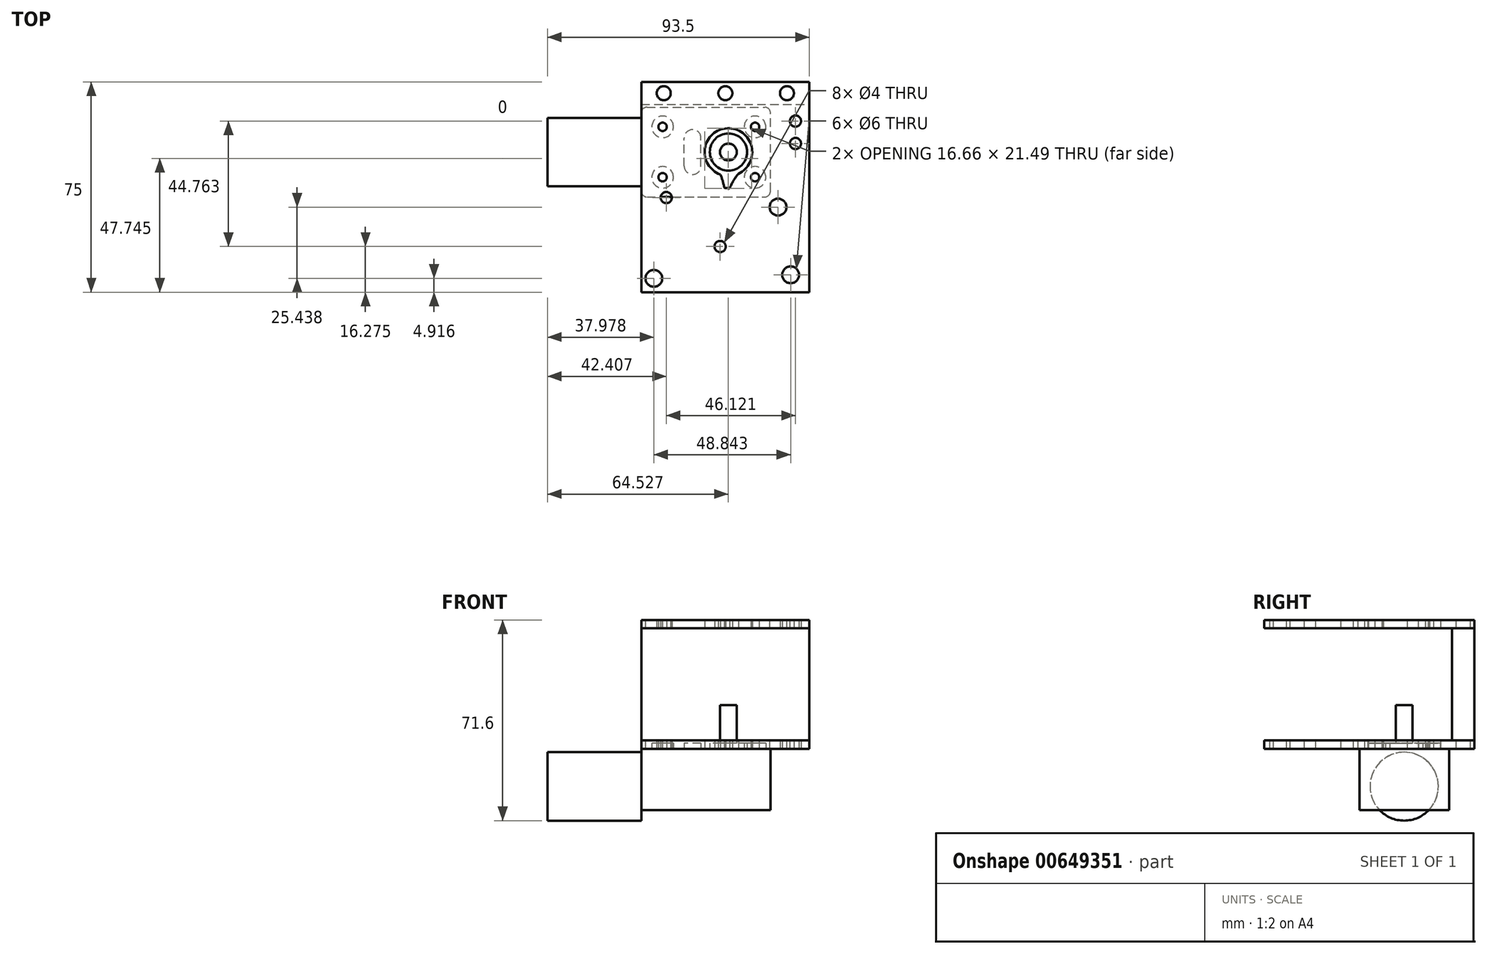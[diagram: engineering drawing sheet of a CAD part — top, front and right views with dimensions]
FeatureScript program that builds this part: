
annotation { "Feature Type Name" : "Feature", "Feature Type Description" : "" }
export const myFeature = defineFeature(function(context is Context, id is Id, definition is map)
    precondition{}
    {
        {
            var Q0;
            Q0=qCreatedBy(makeId("Top.planeOp"),FACE);
            var sketch = newSketch(context, id + "F0", { "sketchPlane" : qUnion([Q0])});
            skCircle(sketch, "E0", {"center": v(0, 0) * mm, "radius": 3 * mm});
            skCircle(sketch, "E1", {"center": v(0, 0) * mm, "radius": 6.65 * mm});
            skLineSegment(sketch, "E2.bottom", {"start": v(-29.1, -16) * mm, "end": v(13, -16) * mm});
            skLineSegment(sketch, "E2.top", {"start": v(-29.1, 16) * mm, "end": v(13, 16) * mm});
            skLineSegment(sketch, "E2.left", {"start": v(-31.1, -14) * mm, "end": v(-31.1, 14) * mm});
            skLineSegment(sketch, "E2.right", {"start": v(15, -14) * mm, "end": v(15, 14) * mm});
            skLineSegment(sketch, "E3", {"start": v(-31.1, 0) * mm, "end": v(15, 0) * mm, "construction": true});
            skLineSegment(sketch, "E4.bottom", {"start": v(-23.5, -9) * mm, "end": v(9.5, -9) * mm, "construction": true});
            skLineSegment(sketch, "E4.top", {"start": v(-23.5, 9) * mm, "end": v(9.5, 9) * mm, "construction": true});
            skLineSegment(sketch, "E4.left", {"start": v(-23.5, -9) * mm, "end": v(-23.5, 9) * mm, "construction": true});
            skLineSegment(sketch, "E4.right", {"start": v(9.5, -9) * mm, "end": v(9.5, 9) * mm, "construction": true});
            skCircle(sketch, "E5", {"center": v(-23.5, 9) * mm, "radius": 1.5 * mm});
            skCircle(sketch, "E6", {"center": v(-23.5, -9) * mm, "radius": 1.5 * mm});
            skCircle(sketch, "E7", {"center": v(9.5, 9) * mm, "radius": 1.5 * mm});
            skCircle(sketch, "E8", {"center": v(9.5, -9) * mm, "radius": 1.5 * mm});
            skCircle(sketch, "E9", {"center": v(-23.5, 9) * mm, "radius": 3.85 * mm});
            skCircle(sketch, "E10", {"center": v(9.5, 9) * mm, "radius": 3.85 * mm});
            skCircle(sketch, "E11", {"center": v(9.5, -9) * mm, "radius": 3.85 * mm});
            skCircle(sketch, "E12", {"center": v(-23.5, -9) * mm, "radius": 3.85 * mm});
            skPoint(sketch, "E13", {"position": v(9.5, 0) * mm});
            skLineSegment(sketch, "E14.left", {"start": v(-15.8, -5) * mm, "end": v(-15.8, 5) * mm});
            skLineSegment(sketch, "E14.right", {"start": v(-9.8, -5) * mm, "end": v(-9.8, 5) * mm});
            skArc(sketch, "E15", {"start": v(-9.8, 5) * mm, "mid": v(-12.8, 8) * mm, "end": v(-15.8, 5) * mm});
            skArc(sketch, "E16", {"start": v(-15.8, -5) * mm, "mid": v(-12.8, -8) * mm, "end": v(-9.8, -5) * mm});
            skPoint(sketch, "E17", {"position": v(-15.8, 0) * mm});
            skPoint(sketch, "E18.visualSharp", {"position": v(15, 16) * mm});
            skArc(sketch, "E18.filletArc", {"start": v(15, 14) * mm, "mid": v(14.41, 15.41) * mm, "end": v(13, 16) * mm});
            skPoint(sketch, "E19.visualSharp", {"position": v(15, -16) * mm});
            skArc(sketch, "E19.filletArc", {"start": v(13, -16) * mm, "mid": v(14.41, -15.41) * mm, "end": v(15, -14) * mm});
            skPoint(sketch, "E20.visualSharp", {"position": v(-31.1, 16) * mm});
            skArc(sketch, "E20.filletArc", {"start": v(-29.1, 16) * mm, "mid": v(-30.51, 15.41) * mm, "end": v(-31.1, 14) * mm});
            skPoint(sketch, "E21.visualSharp", {"position": v(-31.1, -16) * mm});
            skArc(sketch, "E21.filletArc", {"start": v(-31.1, -14) * mm, "mid": v(-30.51, -15.41) * mm, "end": v(-29.1, -16) * mm});
            skSolve(sketch);
        }
        {
            var Q0;
            Q0 = qSketchRegion(id + "F0", true);
            var Q1;
            Q1=makeQuery(id+"F0.imprint","IMPRINT",FACE,{"disambiguationData":[TD([[makeQuery(id+"F0.imprint","IMPRINT",EDGE,{"derivedFrom":sQuery(id+"F0.wireOp",EDGE,"E6")}),-1.0]])]});
            var Q2;
            Q2=makeQuery(id+"F0.imprint","IMPRINT",FACE,{"disambiguationData":[TD([[makeQuery(id+"F0.imprint","IMPRINT",EDGE,{"derivedFrom":sQuery(id+"F0.wireOp",EDGE,"E14.left")}),-1.0]])]});
            var Q3;
            Q3=makeQuery(id+"F0.imprint","IMPRINT",FACE,{"disambiguationData":[TD([[makeQuery(id+"F0.imprint","IMPRINT",EDGE,{"derivedFrom":sQuery(id+"F0.wireOp",EDGE,"E0")}),-1.0]])]});
            var Q4;
            Q4=makeQuery(id+"F0.imprint","IMPRINT",FACE,{"disambiguationData":[TD([[makeQuery(id+"F0.imprint","IMPRINT",EDGE,{"derivedFrom":sQuery(id+"F0.wireOp",EDGE,"E0")}),1.0]])]});
            var Q5;
            Q5=makeQuery(id+"F0.imprint","IMPRINT",FACE,{"disambiguationData":[TD([[makeQuery(id+"F0.imprint","IMPRINT",EDGE,{"derivedFrom":sQuery(id+"F0.wireOp",EDGE,"E7")}),1.0]])]});
            var Q6;
            Q6=makeQuery(id+"F0.imprint","IMPRINT",FACE,{"disambiguationData":[TD([[makeQuery(id+"F0.imprint","IMPRINT",EDGE,{"derivedFrom":sQuery(id+"F0.wireOp",EDGE,"E8")}),-1.0]])]});
            var Q7;
            Q7=makeQuery(id+"F0.imprint","IMPRINT",FACE,{"disambiguationData":[TD([[makeQuery(id+"F0.imprint","IMPRINT",EDGE,{"derivedFrom":sQuery(id+"F0.wireOp",EDGE,"E8")}),1.0]])]});
            var Q8;
            Q8=makeQuery(id+"F0.imprint","IMPRINT",FACE,{"disambiguationData":[TD([[makeQuery(id+"F0.imprint","IMPRINT",EDGE,{"derivedFrom":sQuery(id+"F0.wireOp",EDGE,"E7")}),-1.0]])]});
            var Q9;
            Q9=makeQuery(id+"F0.imprint","IMPRINT",FACE,{"disambiguationData":[TD([[makeQuery(id+"F0.imprint","IMPRINT",EDGE,{"derivedFrom":sQuery(id+"F0.wireOp",EDGE,"E5")}),-1.0]])]});
            var Q10;
            Q10=makeQuery(id+"F0.imprint","IMPRINT",FACE,{"disambiguationData":[TD([[makeQuery(id+"F0.imprint","IMPRINT",EDGE,{"derivedFrom":sQuery(id+"F0.wireOp",EDGE,"E6")}),1.0]])]});
            var Q11;
            Q11=makeQuery(id+"F0.imprint","IMPRINT",FACE,{"disambiguationData":[TD([[makeQuery(id+"F0.imprint","IMPRINT",EDGE,{"derivedFrom":sQuery(id+"F0.wireOp",EDGE,"E5")}),1.0]])]});
            extrude(context, id + "F1", {"entities" : qUnion([Q0, Q1, Q2, Q3, Q4, Q5, Q6, Q7, Q8, Q9, Q10, Q11]), "oppositeDirection" : true, "depth" : 21.8 * mm, "offsetDistance" : 25 * mm});
        }
        {
            var Q0;
            Q0=makeQuery(id+"F0.imprint","IMPRINT",FACE,{"disambiguationData":[TD([[makeQuery(id+"F0.imprint","IMPRINT",EDGE,{"derivedFrom":sQuery(id+"F0.wireOp",EDGE,"E6")}),-1.0]])]});
            var Q1;
            Q1=makeQuery(id+"F0.imprint","IMPRINT",FACE,{"disambiguationData":[TD([[makeQuery(id+"F0.imprint","IMPRINT",EDGE,{"derivedFrom":sQuery(id+"F0.wireOp",EDGE,"E5")}),-1.0]])]});
            var Q2;
            Q2=makeQuery(id+"F0.imprint","IMPRINT",FACE,{"disambiguationData":[TD([[makeQuery(id+"F0.imprint","IMPRINT",EDGE,{"derivedFrom":sQuery(id+"F0.wireOp",EDGE,"E14.left")}),-1.0]])]});
            var Q3;
            Q3=makeQuery(id+"F0.imprint","IMPRINT",FACE,{"disambiguationData":[TD([[makeQuery(id+"F0.imprint","IMPRINT",EDGE,{"derivedFrom":sQuery(id+"F0.wireOp",EDGE,"E0")}),-1.0]])]});
            var Q4;
            Q4=makeQuery(id+"F0.imprint","IMPRINT",FACE,{"disambiguationData":[TD([[makeQuery(id+"F0.imprint","IMPRINT",EDGE,{"derivedFrom":sQuery(id+"F0.wireOp",EDGE,"E7")}),-1.0]])]});
            var Q5;
            Q5=makeQuery(id+"F0.imprint","IMPRINT",FACE,{"disambiguationData":[TD([[makeQuery(id+"F0.imprint","IMPRINT",EDGE,{"derivedFrom":sQuery(id+"F0.wireOp",EDGE,"E8")}),-1.0]])]});
            extrude(context, id + "F2", {"entities" : qUnion([Q0, Q1, Q2, Q3, Q4, Q5]), "operationType" : NewBodyOperationType.ADD, "depth" : 2 * mm, "offsetDistance" : 25 * mm});
        }
        {
            var Q0;
            Q0=makeQuery(id+"F0.imprint","IMPRINT",FACE,{"disambiguationData":[TD([[makeQuery(id+"F0.imprint","IMPRINT",EDGE,{"derivedFrom":sQuery(id+"F0.wireOp",EDGE,"E0")}),1.0]])]});
            extrude(context, id + "F3", {"entities" : qUnion([Q0]), "operationType" : NewBodyOperationType.ADD, "depth" : 15.6 * mm, "offsetDistance" : 25 * mm});
        }
        {
            var Q0;
            Q0=makeQuery(id+"F1.opExtrude","SWEPT_FACE",FACE,{"disambiguationData":[OSD([sQuery(id+"F0.wireOp",EDGE,"E2.left")])]});
            var sketch = newSketch(context, id + "F4", { "sketchPlane" : qUnion([Q0])});
            skLineSegment(sketch, "E22", {"start": v(0, 0) * mm, "end": v(0, -21.8) * mm, "construction": true});
            skCircle(sketch, "E23", {"center": v(0, -13.4) * mm, "radius": 12.2 * mm});
            skSolve(sketch);
        }
        {
            var Q0;
            Q0 = qSketchRegion(id + "F4", true);
            extrude(context, id + "F5", {"entities" : qUnion([Q0]), "operationType" : NewBodyOperationType.ADD, "depth" : 33.5 * mm, "offsetDistance" : 25 * mm});
        }
        {
            var Q0;
            Q0=qCreatedBy(makeId("Top.planeOp"),FACE);
            var sketch = newSketch(context, id + "F6", { "sketchPlane" : qUnion([Q0])});
            skCircle(sketch, "E24", {"center": v(0, 0) * mm, "radius": 8.5 * mm});
            skCircle(sketch, "E25.0", {"center": v(9.5, 9) * mm, "radius": 1.5 * mm});
            skCircle(sketch, "E25.1", {"center": v(9.5, -9) * mm, "radius": 1.5 * mm});
            skCircle(sketch, "E25.2", {"center": v(-23.5, -9) * mm, "radius": 1.5 * mm});
            skCircle(sketch, "E25.3", {"center": v(-23.5, 9) * mm, "radius": 1.5 * mm});
            skLineSegment(sketch, "E26.bottom", {"start": v(-31.1, 25) * mm, "end": v(28.9, 25) * mm});
            skLineSegment(sketch, "E26.top", {"start": v(-31.1, -50) * mm, "end": v(28.9, -50) * mm});
            skLineSegment(sketch, "E26.left", {"start": v(-31.1, 25) * mm, "end": v(-31.1, -50) * mm});
            skLineSegment(sketch, "E26.right", {"start": v(28.9, 25) * mm, "end": v(28.9, -50) * mm});
            skLineSegment(sketch, "E27.top", {"start": v(-31.1, 17) * mm, "end": v(28.9, 17) * mm});
            skLineSegment(sketch, "E27.left", {"start": v(-31.1, 25) * mm, "end": v(-31.1, 17) * mm});
            skLineSegment(sketch, "E27.right", {"start": v(28.9, 25) * mm, "end": v(28.9, 17) * mm});
            skCircle(sketch, "E28", {"center": v(9.5, 9) * mm, "radius": 2 * mm, "construction": true});
            skCircle(sketch, "E29", {"center": v(9.5, -9) * mm, "radius": 2 * mm, "construction": true});
            skCircle(sketch, "E30", {"center": v(-23.5, 9) * mm, "radius": 2 * mm, "construction": true});
            skCircle(sketch, "E31", {"center": v(-23.5, -9) * mm, "radius": 2 * mm, "construction": true});
            skLineSegment(sketch, "E32.0", {"start": v(-29.1, 16) * mm, "end": v(13, 16) * mm});
            skArc(sketch, "E32.1", {"start": v(15, 14) * mm, "mid": v(14.41, 15.41) * mm, "end": v(13, 16) * mm});
            skLineSegment(sketch, "E32.2", {"start": v(15, -14) * mm, "end": v(15, 14) * mm});
            skArc(sketch, "E32.3", {"start": v(13, -16) * mm, "mid": v(14.41, -15.41) * mm, "end": v(15, -14) * mm});
            skLineSegment(sketch, "E32.4", {"start": v(-29.1, -16) * mm, "end": v(13, -16) * mm});
            skArc(sketch, "E32.5", {"start": v(-31.1, -14) * mm, "mid": v(-30.51, -15.41) * mm, "end": v(-29.1, -16) * mm});
            skLineSegment(sketch, "E32.6", {"start": v(-31.1, -14) * mm, "end": v(-31.1, 14) * mm});
            skArc(sketch, "E32.7", {"start": v(-29.1, 16) * mm, "mid": v(-30.51, 15.41) * mm, "end": v(-31.1, 14) * mm});
            skCircle(sketch, "E33", {"center": v(0, 0) * mm, "radius": 27.5 * mm, "construction": true});
            skCircle(sketch, "E34", {"center": v(-22.2, -16.24) * mm, "radius": 26 * mm, "construction": true});
            skCircle(sketch, "E35", {"center": v(-22.2, -16.24) * mm, "radius": 21 * mm});
            skLineSegment(sketch, "E36", {"start": v(-31.1, 16) * mm, "end": v(28.9, 16) * mm, "construction": true});
            skCircle(sketch, "E37", {"center": v(-2.95, -33.73) * mm, "radius": 21 * mm});
            skCircle(sketch, "E38", {"center": v(17.7, -19.65) * mm, "radius": 18.5 * mm});
            skCircle(sketch, "E39", {"center": v(17.7, -19.65) * mm, "radius": 27.5 * mm, "construction": true});
            skCircle(sketch, "E40", {"center": v(45.2, -20.4) * mm, "radius": 11 * mm});
            skCircle(sketch, "E41", {"center": v(-22.2, -16.24) * mm, "radius": 2 * mm});
            skCircle(sketch, "E42", {"center": v(-2.95, -33.73) * mm, "radius": 2 * mm});
            skCircle(sketch, "E43", {"center": v(17.7, -19.65) * mm, "radius": 3 * mm});
            skCircle(sketch, "E44", {"center": v(45.2, -20.4) * mm, "radius": 5 * mm});
            skCircle(sketch, "E45", {"center": v(-22.2, -16.24) * mm, "radius": 7 * mm, "construction": true});
            skCircle(sketch, "E46", {"center": v(-2.95, -33.73) * mm, "radius": 8.5 * mm, "construction": true});
            skCircle(sketch, "E47", {"center": v(-26.62, -45.08) * mm, "radius": 3 * mm});
            skCircle(sketch, "E48", {"center": v(-26.62, -45.08) * mm, "radius": 5 * mm, "construction": true});
            skCircle(sketch, "E49", {"center": v(22.22, -43.81) * mm, "radius": 3 * mm});
            skCircle(sketch, "E50", {"center": v(22.22, -43.81) * mm, "radius": 5 * mm, "construction": true});
            skPoint(sketch, "E51", {"position": v(28.9, -12.5) * mm});
            skCircle(sketch, "E52", {"center": v(-2.95, -33.73) * mm, "radius": 25 * mm, "construction": true});
            skCircle(sketch, "E53", {"center": v(17.7, -19.65) * mm, "radius": 7 * mm, "construction": true});
            skCircle(sketch, "E54", {"center": v(23.93, 11.04) * mm, "radius": 2 * mm});
            skCircle(sketch, "E55", {"center": v(23.93, 3.04) * mm, "radius": 2 * mm});
            skLineSegment(sketch, "E56", {"start": v(28.9, -1.15) * mm, "end": v(11.67, -1.15) * mm, "construction": true});
            skLineSegment(sketch, "E57", {"start": v(-31.1, 21) * mm, "end": v(28.9, 21) * mm, "construction": true});
            skCircle(sketch, "E58", {"center": v(-1.1, 21) * mm, "radius": 2.5 * mm});
            skCircle(sketch, "E59", {"center": v(-23.1, 21) * mm, "radius": 2.5 * mm});
            skCircle(sketch, "E60", {"center": v(20.9, 21) * mm, "radius": 2.5 * mm});
            skSolve(sketch);
        }
        {
            var Q0;
            Q0=makeQuery(id+"F6.imprint","IMPRINT",FACE,{"disambiguationData":[TD([[makeQuery(id+"F6.imprint","IMPRINT",EDGE,{"derivedFrom":sQuery(id+"F6.wireOp",EDGE,"E26.bottom")}),-1.0]])]});
            var Q1;
            {var subQ6=sQuery(id+"F6.wireOp",EDGE,"E27.top");Q1=makeQuery(id+"F6.imprint","IMPRINT",FACE,{"disambiguationData":[TD([[makeQuery(id+"F6.imprint","IMPRINT",EDGE,{"derivedFrom":subQ6}),-1.0]])]});}
            var Q2;
            {var subQ3=sQuery(id+"F6.wireOp",EDGE,"E38");var subQ5=sQuery(id+"F6.wireOp",EDGE,"E26.right");var subQ6=makeQuery(id+"F6.imprint","INTERSECT",VERTEX,{"disambiguationData":[OD(0.0)],"derivedFrom":[subQ5,subQ3]});Q2=makeQuery(id+"F6.imprint","IMPRINT",FACE,{"disambiguationData":[TD([[makeQuery(id+"F6.imprint","IMPRINT",EDGE,{"disambiguationData":[TD([[subQ6,-1.0]])],"derivedFrom":subQ5}),-1.0]])]});}
            var Q3;
            {var subQ5=sQuery(id+"F6.wireOp",EDGE,"E26.top");Q3=makeQuery(id+"F6.imprint","IMPRINT",FACE,{"disambiguationData":[TD([[makeQuery(id+"F6.imprint","IMPRINT",EDGE,{"derivedFrom":subQ5}),1.0]])]});}
            var Q4;
            Q4=makeQuery(id+"F6.imprint","IMPRINT",FACE,{"disambiguationData":[TD([[makeQuery(id+"F6.imprint","IMPRINT",EDGE,{"derivedFrom":sQuery(id+"F6.wireOp",EDGE,"E25.0")}),-1.0]])]});
            var Q5;
            {var subQ1=sQuery(id+"F6.wireOp",EDGE,"E35");var subQ5=sQuery(id+"F6.wireOp",EDGE,"E32.4");var subQ6=makeQuery(id+"F6.imprint","INTERSECT",VERTEX,{"derivedFrom":[subQ5,subQ1]});Q5=makeQuery(id+"F6.imprint","IMPRINT",FACE,{"disambiguationData":[TD([[makeQuery(id+"F6.imprint","IMPRINT",EDGE,{"disambiguationData":[TD([[subQ6,-1.0]])],"derivedFrom":subQ5}),-1.0]])]});}
            var Q6;
            {var subQ1=sQuery(id+"F6.wireOp",EDGE,"E32.3");Q6=makeQuery(id+"F6.imprint","IMPRINT",FACE,{"disambiguationData":[TD([[makeQuery(id+"F6.imprint","IMPRINT",EDGE,{"derivedFrom":subQ1}),-1.0]])]});}
            var Q7;
            Q7=makeQuery(id+"F6.imprint","IMPRINT",FACE,{"disambiguationData":[TD([[makeQuery(id+"F6.imprint","IMPRINT",EDGE,{"derivedFrom":sQuery(id+"F6.wireOp",EDGE,"E41")}),-1.0]])]});
            var Q8;
            {var subQ0=sQuery(id+"F6.wireOp",EDGE,"E37");var subQ1=sQuery(id+"F6.wireOp",EDGE,"E35");var subQ2=makeQuery(id+"F6.imprint","INTERSECT",VERTEX,{"disambiguationData":[OD(1.0)],"derivedFrom":[subQ1,subQ0]});Q8=makeQuery(id+"F6.imprint","IMPRINT",FACE,{"disambiguationData":[TD([[makeQuery(id+"F6.imprint","IMPRINT",EDGE,{"disambiguationData":[TD([[subQ2,-1.0]])],"derivedFrom":subQ1}),-1.0]])]});}
            var Q9;
            Q9=makeQuery(id+"F6.imprint","IMPRINT",FACE,{"disambiguationData":[TD([[makeQuery(id+"F6.imprint","IMPRINT",EDGE,{"derivedFrom":sQuery(id+"F6.wireOp",EDGE,"E42")}),-1.0]])]});
            var Q10;
            {var subQ1=sQuery(id+"F6.wireOp",EDGE,"E37");var subQ5=sQuery(id+"F6.wireOp",EDGE,"E43");var subQ6=makeQuery(id+"F6.imprint","INTERSECT",VERTEX,{"disambiguationData":[OD(0.0)],"derivedFrom":[subQ1,subQ5]});Q10=makeQuery(id+"F6.imprint","IMPRINT",FACE,{"disambiguationData":[TD([[makeQuery(id+"F6.imprint","IMPRINT",EDGE,{"disambiguationData":[TD([[subQ6,-1.0]])],"derivedFrom":subQ1}),1.0]])]});}
            var Q11;
            {var subQ0=sQuery(id+"F6.wireOp",EDGE,"E46");var subQ1=sQuery(id+"F6.wireOp",EDGE,"E38");var subQ2=makeQuery(id+"F6.imprint","INTERSECT",VERTEX,{"disambiguationData":[OD(0.0)],"derivedFrom":[subQ1,subQ0]});Q11=makeQuery(id+"F6.imprint","IMPRINT",FACE,{"disambiguationData":[TD([[makeQuery(id+"F6.imprint","IMPRINT",EDGE,{"disambiguationData":[TD([[subQ2,-1.0]])],"derivedFrom":subQ1}),1.0]])]});}
            var Q12;
            {var subQ0=sQuery(id+"F6.wireOp",EDGE,"E46");var subQ1=sQuery(id+"F6.wireOp",EDGE,"E35");var subQ2=makeQuery(id+"F6.imprint","INTERSECT",VERTEX,{"disambiguationData":[OD(0.0)],"derivedFrom":[subQ1,subQ0]});Q12=makeQuery(id+"F6.imprint","IMPRINT",FACE,{"disambiguationData":[TD([[makeQuery(id+"F6.imprint","IMPRINT",EDGE,{"disambiguationData":[TD([[subQ2,1.0]])],"derivedFrom":subQ1}),1.0]])]});}
            var Q13;
            {var subQ5=sQuery(id+"F6.wireOp",EDGE,"E35");var subQ6=sQuery(id+"F6.wireOp",EDGE,"E32.2");var subQ7=makeQuery(id+"F6.imprint","INTERSECT",VERTEX,{"derivedFrom":[subQ6,subQ5]});Q13=makeQuery(id+"F6.imprint","IMPRINT",FACE,{"disambiguationData":[TD([[makeQuery(id+"F6.imprint","IMPRINT",EDGE,{"disambiguationData":[TD([[subQ7,-1.0]])],"derivedFrom":subQ6}),-1.0]])]});}
            var Q14;
            {var subQ5=sQuery(id+"F6.wireOp",EDGE,"E32.3");Q14=makeQuery(id+"F6.imprint","IMPRINT",FACE,{"disambiguationData":[TD([[makeQuery(id+"F6.imprint","IMPRINT",EDGE,{"derivedFrom":subQ5}),1.0]])]});}
            var Q15;
            {var subQ0=sQuery(id+"F6.wireOp",EDGE,"E35");var subQ1=sQuery(id+"F6.wireOp",EDGE,"E32.2");var subQ2=makeQuery(id+"F6.imprint","INTERSECT",VERTEX,{"derivedFrom":[subQ1,subQ0]});Q15=makeQuery(id+"F6.imprint","IMPRINT",FACE,{"disambiguationData":[TD([[makeQuery(id+"F6.imprint","IMPRINT",EDGE,{"disambiguationData":[TD([[subQ2,-1.0]])],"derivedFrom":subQ1}),1.0]])]});}
            var Q16;
            {var subQ0=sQuery(id+"F6.wireOp",EDGE,"E35");var subQ8=sQuery(id+"F6.wireOp",EDGE,"E24");var subQ11=makeQuery(id+"F6.imprint","INTERSECT",VERTEX,{"disambiguationData":[OD(0.0)],"derivedFrom":[subQ8,subQ0]});Q16=makeQuery(id+"F6.imprint","IMPRINT",FACE,{"disambiguationData":[TD([[makeQuery(id+"F6.imprint","IMPRINT",EDGE,{"disambiguationData":[TD([[subQ11,1.0]])],"derivedFrom":subQ8}),-1.0]])]});}
            var Q17;
            {var subQ0=sQuery(id+"F6.wireOp",EDGE,"E45");var subQ1=sQuery(id+"F6.wireOp",EDGE,"E37");var subQ2=makeQuery(id+"F6.imprint","INTERSECT",VERTEX,{"disambiguationData":[OD(0.0)],"derivedFrom":[subQ1,subQ0]});Q17=makeQuery(id+"F6.imprint","IMPRINT",FACE,{"disambiguationData":[TD([[makeQuery(id+"F6.imprint","IMPRINT",EDGE,{"disambiguationData":[TD([[subQ2,-1.0]])],"derivedFrom":subQ1}),1.0]])]});}
            var Q18;
            {var subQ0=sQuery(id+"F6.wireOp",EDGE,"E32.5");Q18=makeQuery(id+"F6.imprint","IMPRINT",FACE,{"disambiguationData":[TD([[makeQuery(id+"F6.imprint","IMPRINT",EDGE,{"derivedFrom":subQ0}),-1.0]])]});}
            var Q19;
            {var subQ0=sQuery(id+"F6.wireOp",EDGE,"E45");var subQ1=sQuery(id+"F6.wireOp",EDGE,"E32.4");var subQ2=makeQuery(id+"F6.imprint","INTERSECT",VERTEX,{"disambiguationData":[OD(1.0)],"derivedFrom":[subQ1,subQ0]});Q19=makeQuery(id+"F6.imprint","IMPRINT",FACE,{"disambiguationData":[TD([[makeQuery(id+"F6.imprint","IMPRINT",EDGE,{"disambiguationData":[TD([[subQ2,-1.0]])],"derivedFrom":subQ1}),-1.0]])]});}
            var Q20;
            {var subQ0=sQuery(id+"F6.wireOp",EDGE,"E37");var subQ1=sQuery(id+"F6.wireOp",EDGE,"E32.4");var subQ2=makeQuery(id+"F6.imprint","INTERSECT",VERTEX,{"derivedFrom":[subQ1,subQ0]});Q20=makeQuery(id+"F6.imprint","IMPRINT",FACE,{"disambiguationData":[TD([[makeQuery(id+"F6.imprint","IMPRINT",EDGE,{"disambiguationData":[TD([[subQ2,-1.0]])],"derivedFrom":subQ1}),1.0]])]});}
            var Q21;
            {var subQ0=sQuery(id+"F6.wireOp",EDGE,"E35");var subQ1=sQuery(id+"F6.wireOp",EDGE,"E32.4");var subQ2=makeQuery(id+"F6.imprint","INTERSECT",VERTEX,{"derivedFrom":[subQ1,subQ0]});Q21=makeQuery(id+"F6.imprint","IMPRINT",FACE,{"disambiguationData":[TD([[makeQuery(id+"F6.imprint","IMPRINT",EDGE,{"disambiguationData":[TD([[subQ2,-1.0]])],"derivedFrom":subQ1}),1.0]])]});}
            var Q22;
            {var subQ0=sQuery(id+"F6.wireOp",EDGE,"E46");var subQ1=sQuery(id+"F6.wireOp",EDGE,"E35");var subQ2=makeQuery(id+"F6.imprint","INTERSECT",VERTEX,{"disambiguationData":[OD(0.0)],"derivedFrom":[subQ1,subQ0]});Q22=makeQuery(id+"F6.imprint","IMPRINT",FACE,{"disambiguationData":[TD([[makeQuery(id+"F6.imprint","IMPRINT",EDGE,{"disambiguationData":[TD([[subQ2,-1.0]])],"derivedFrom":subQ1}),1.0]])]});}
            var Q23;
            {var subQ0=sQuery(id+"F6.wireOp",EDGE,"E45");var subQ1=sQuery(id+"F6.wireOp",EDGE,"E32.4");var subQ2=makeQuery(id+"F6.imprint","INTERSECT",VERTEX,{"disambiguationData":[OD(0.0)],"derivedFrom":[subQ1,subQ0]});Q23=makeQuery(id+"F6.imprint","IMPRINT",FACE,{"disambiguationData":[TD([[makeQuery(id+"F6.imprint","IMPRINT",EDGE,{"disambiguationData":[TD([[subQ2,-1.0]])],"derivedFrom":subQ1}),1.0]])]});}
            var Q24;
            {var subQ0=sQuery(id+"F6.wireOp",EDGE,"E40");var subQ1=sQuery(id+"F6.wireOp",EDGE,"E26.right");var subQ2=makeQuery(id+"F6.imprint","INTERSECT",VERTEX,{"disambiguationData":[OD(0.0)],"derivedFrom":[subQ1,subQ0]});Q24=makeQuery(id+"F6.imprint","IMPRINT",FACE,{"disambiguationData":[TD([[makeQuery(id+"F6.imprint","IMPRINT",EDGE,{"disambiguationData":[TD([[subQ2,-1.0]])],"derivedFrom":subQ1}),-1.0]])]});}
            var Q25;
            {var subQ0=sQuery(id+"F6.wireOp",EDGE,"E38");var subQ1=sQuery(id+"F6.wireOp",EDGE,"E32.4");var subQ2=makeQuery(id+"F6.imprint","INTERSECT",VERTEX,{"derivedFrom":[subQ1,subQ0]});Q25=makeQuery(id+"F6.imprint","IMPRINT",FACE,{"disambiguationData":[TD([[makeQuery(id+"F6.imprint","IMPRINT",EDGE,{"disambiguationData":[TD([[subQ2,-1.0]])],"derivedFrom":subQ1}),1.0]])]});}
            var Q26;
            {var subQ0=sQuery(id+"F6.wireOp",EDGE,"E38");var subQ1=sQuery(id+"F6.wireOp",EDGE,"E32.4");var subQ2=makeQuery(id+"F6.imprint","INTERSECT",VERTEX,{"derivedFrom":[subQ1,subQ0]});Q26=makeQuery(id+"F6.imprint","IMPRINT",FACE,{"disambiguationData":[TD([[makeQuery(id+"F6.imprint","IMPRINT",EDGE,{"disambiguationData":[TD([[subQ2,-1.0]])],"derivedFrom":subQ1}),-1.0]])]});}
            var Q27;
            {var subQ0=sQuery(id+"F6.wireOp",EDGE,"E37");var subQ1=sQuery(id+"F6.wireOp",EDGE,"E32.4");var subQ2=makeQuery(id+"F6.imprint","INTERSECT",VERTEX,{"disambiguationData":[OD(0.0)],"derivedFrom":[subQ1,subQ0]});Q27=makeQuery(id+"F6.imprint","IMPRINT",FACE,{"disambiguationData":[TD([[makeQuery(id+"F6.imprint","IMPRINT",EDGE,{"disambiguationData":[TD([[subQ2,-1.0]])],"derivedFrom":subQ1}),-1.0]])]});}
            extrude(context, id + "F7", {"entities" : qUnion([Q0, Q1, Q2, Q3, Q4, Q5, Q6, Q7, Q8, Q9, Q10, Q11, Q12, Q13, Q14, Q15, Q16, Q17, Q18, Q19, Q20, Q21, Q22, Q23, Q24, Q25, Q26, Q27]), "depth" : 3 * mm, "offsetDistance" : 25 * mm});
        }
        {
            var Q0;
            Q0=makeQuery(id+"F7.opExtrude","CAP_FACE",FACE,{"disambiguationData":[OSD([sQuery(id+"F6.wireOp",EDGE,"E24"),sQuery(id+"F6.wireOp",EDGE,"E25.0"),sQuery(id+"F6.wireOp",EDGE,"E25.1"),sQuery(id+"F6.wireOp",EDGE,"E25.2"),sQuery(id+"F6.wireOp",EDGE,"E25.3"),sQuery(id+"F6.wireOp",EDGE,"E26.top"),sQuery(id+"F6.wireOp",EDGE,"E26.left"),sQuery(id+"F6.wireOp",EDGE,"E26.right"),sQuery(id+"F6.wireOp",EDGE,"E26.bottom"),sQuery(id+"F6.wireOp",EDGE,"E27.left"),sQuery(id+"F6.wireOp",EDGE,"E27.right"),sQuery(id+"F6.wireOp",EDGE,"E32.6"),sQuery(id+"F6.wireOp",EDGE,"E41"),sQuery(id+"F6.wireOp",EDGE,"E42"),sQuery(id+"F6.wireOp",EDGE,"E43"),sQuery(id+"F6.wireOp",EDGE,"E47"),sQuery(id+"F6.wireOp",EDGE,"E49")])],"isStart":false});
            var sketch = newSketch(context, id + "F8", { "sketchPlane" : qUnion([Q0])});
            skLineSegment(sketch, "E61.bottom", {"start": v(-31.1, 25) * mm, "end": v(28.9, 25) * mm});
            skLineSegment(sketch, "E61.top", {"start": v(-31.1, 17) * mm, "end": v(28.9, 17) * mm});
            skLineSegment(sketch, "E61.left", {"start": v(-31.1, 25) * mm, "end": v(-31.1, 17) * mm});
            skLineSegment(sketch, "E61.right", {"start": v(28.9, 25) * mm, "end": v(28.9, 17) * mm});
            skSolve(sketch);
        }
        {
            var Q0;
            Q0 = qSketchRegion(id + "F8", true);
            extrude(context, id + "F9", {"entities" : qUnion([Q0]), "depth" : 40 * mm, "offsetDistance" : 25 * mm});
        }
        {
            var Q0;
            Q0=makeQuery(id+"F7.opExtrude","SWEPT_BODY",BODY,{"disambiguationData":[OSD([sQuery(id+"F6.wireOp",EDGE,"E24"),sQuery(id+"F6.wireOp",EDGE,"E25.0"),sQuery(id+"F6.wireOp",EDGE,"E25.1"),sQuery(id+"F6.wireOp",EDGE,"E25.2"),sQuery(id+"F6.wireOp",EDGE,"E25.3"),sQuery(id+"F6.wireOp",EDGE,"E26.top"),sQuery(id+"F6.wireOp",EDGE,"E26.left"),sQuery(id+"F6.wireOp",EDGE,"E26.right"),sQuery(id+"F6.wireOp",EDGE,"E26.bottom"),sQuery(id+"F6.wireOp",EDGE,"E27.left"),sQuery(id+"F6.wireOp",EDGE,"E27.right"),sQuery(id+"F6.wireOp",EDGE,"E32.6"),sQuery(id+"F6.wireOp",EDGE,"E41"),sQuery(id+"F6.wireOp",EDGE,"E42"),sQuery(id+"F6.wireOp",EDGE,"E43"),sQuery(id+"F6.wireOp",EDGE,"E47"),sQuery(id+"F6.wireOp",EDGE,"E49")])]});
            var Q1;
            Q1=makeQuery(id+"F9.opExtrude","SWEPT_EDGE",EDGE,{"disambiguationData":[OSD([sQuery(id+"F6.wireOp",EDGE,"E26.left"),sQuery(id+"F6.wireOp",EDGE,"E27.left"),sQuery(id+"F6.wireOp",EDGE,"E32.6"),sQuery(id+"F8.wireOp",EDGE,"E61.top"),sQuery(id+"F8.wireOp",EDGE,"E61.left")])]});
            transform(context, id + "F10", {"entities" : qUnion([Q0]), "transformType" : TransformType.TRANSLATION_3D, "dx" : 0 * mm, "dy" : 0 * mm, "dz" : 43 * mm, "makeCopy" : true});
        }
    });
